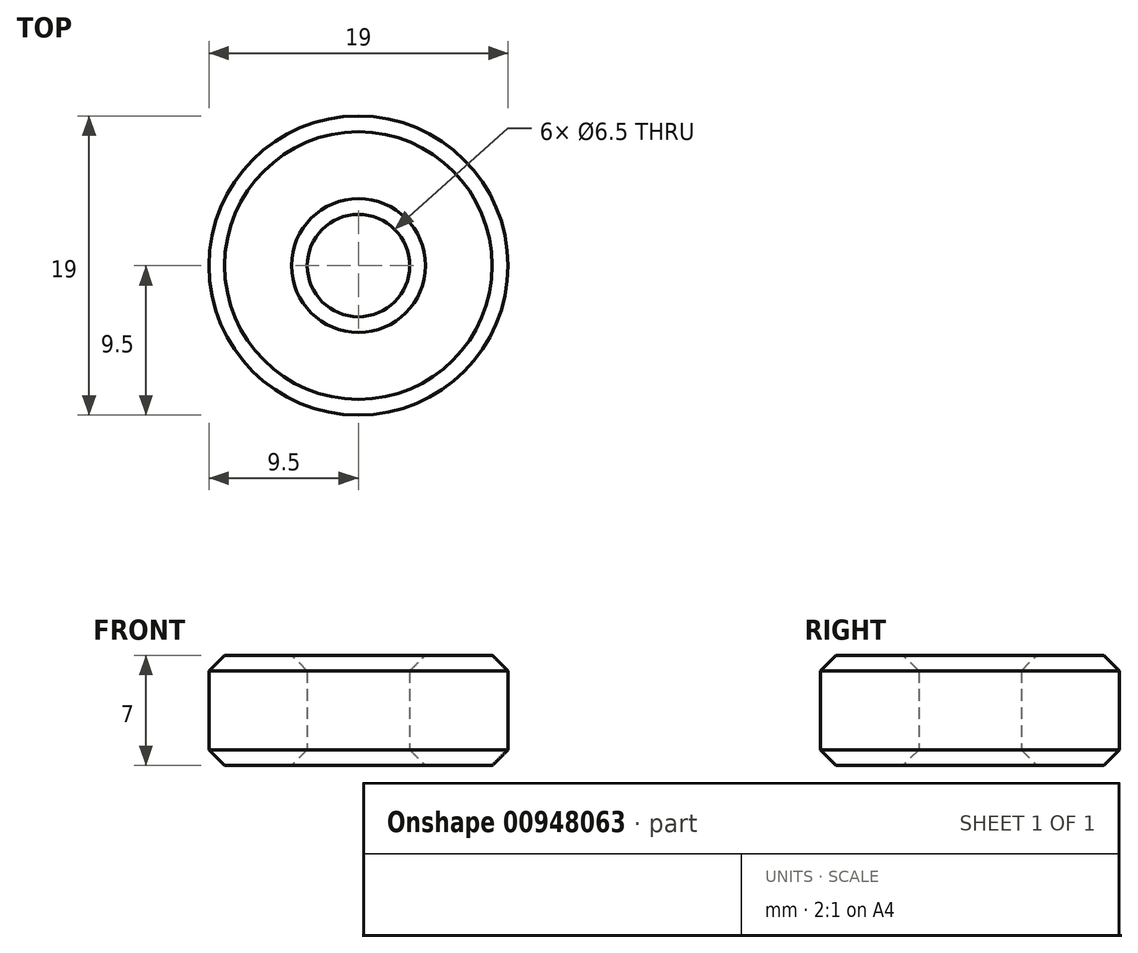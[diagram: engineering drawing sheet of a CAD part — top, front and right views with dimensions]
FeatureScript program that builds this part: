
annotation { "Feature Type Name" : "Feature", "Feature Type Description" : "" }
export const myFeature = defineFeature(function(context is Context, id is Id, definition is map)
    precondition{}
    {
        {
            var Q0;
            Q0=qCreatedBy(makeId("Top.planeOp"),FACE);
            var sketch = newSketch(context, id + "F0", { "sketchPlane" : qUnion([Q0])});
            skCircle(sketch, "E0", {"center": v(0, 0) * mm, "radius": 9.5 * mm});
            skCircle(sketch, "E1", {"center": v(0, 0) * mm, "radius": 3.25 * mm});
            skSolve(sketch);
        }
        {
            var Q0;
            Q0=makeQuery(id+"F0.imprint","IMPRINT",FACE,{"disambiguationData":[TD([[makeQuery(id+"F0.imprint","IMPRINT",EDGE,{"derivedFrom":sQuery(id+"F0.wireOp",EDGE,"E0")}),1.0]])]});
            extrude(context, id + "F1", {"entities" : qUnion([Q0]), "depth" : 7 * mm, "offsetDistance" : 25 * mm});
        }
        {
            var Q0;
            Q0=makeQuery(id+"F1.opExtrude","CAP_EDGE",EDGE,{"disambiguationData":[OSD([sQuery(id+"F0.wireOp",EDGE,"E1")])],"isStart":false});
            var Q1;
            Q1=makeQuery(id+"F1.opExtrude","CAP_EDGE",EDGE,{"disambiguationData":[OSD([sQuery(id+"F0.wireOp",EDGE,"E1")])],"isStart":true});
            var Q2;
            Q2=makeQuery(id+"F1.opExtrude","CAP_EDGE",EDGE,{"disambiguationData":[OSD([sQuery(id+"F0.wireOp",EDGE,"E0")])],"isStart":true});
            var Q3;
            Q3=makeQuery(id+"F1.opExtrude","CAP_EDGE",EDGE,{"disambiguationData":[OSD([sQuery(id+"F0.wireOp",EDGE,"E0")])],"isStart":false});
            chamfer(context, id + "F2", {"entities" : qUnion([Q0, Q1, Q2, Q3]), "width" : 1 * mm, "tangentPropagation" : true});
        }
    });
